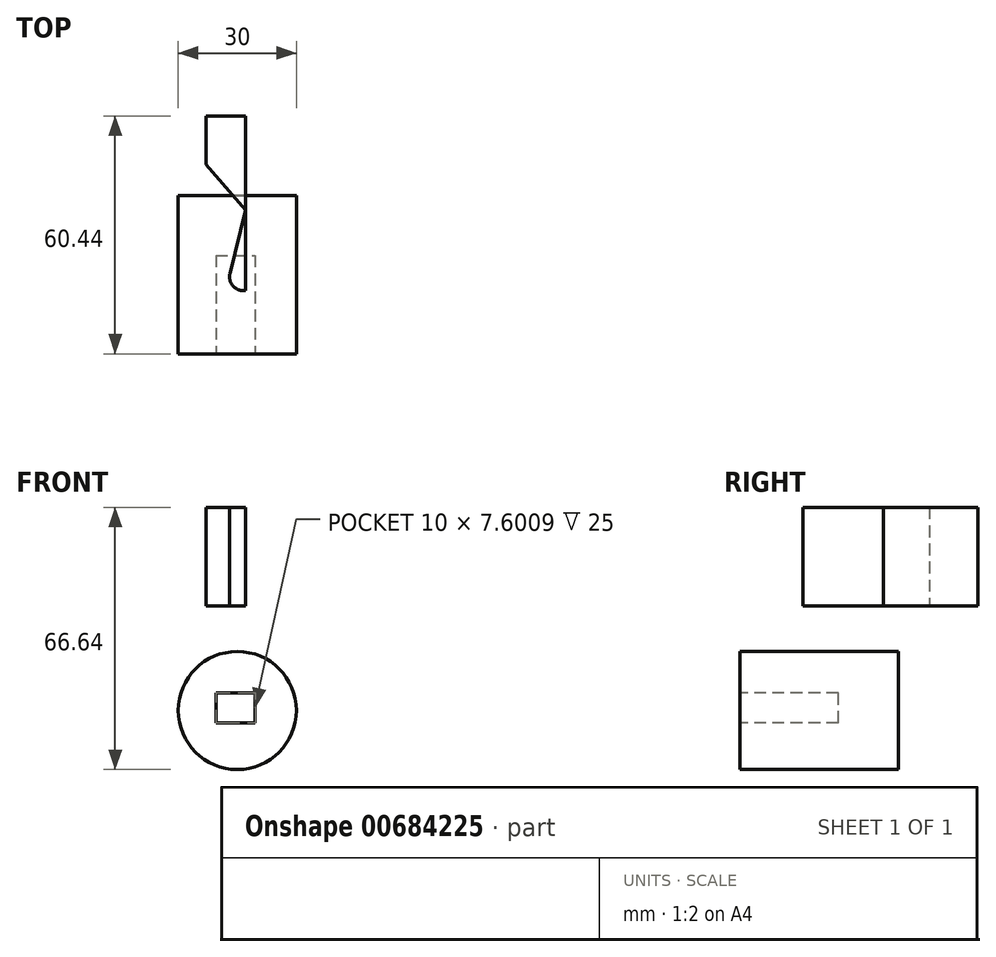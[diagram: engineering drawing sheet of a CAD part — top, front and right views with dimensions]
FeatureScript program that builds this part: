
annotation { "Feature Type Name" : "Feature", "Feature Type Description" : "" }
export const myFeature = defineFeature(function(context is Context, id is Id, definition is map)
    precondition{}
    {
        {
            var Q0;
            Q0=qCreatedBy(makeId("Top.planeOp"),FACE);
            var sketch = newSketch(context, id + "F0", { "sketchPlane" : qUnion([Q0])});
            skLineSegment(sketch, "E0.bottom", {"start": v(-77.17, 20.24) * mm, "end": v(-67.17, 20.24) * mm});
            skLineSegment(sketch, "E0.top", {"start": v(-77.17, -24.16) * mm, "end": v(-67.17, -24.16) * mm});
            skLineSegment(sketch, "E0.left", {"start": v(-77.17, 20.24) * mm, "end": v(-77.17, -24.16) * mm});
            skLineSegment(sketch, "E0.right", {"start": v(-67.17, 20.24) * mm, "end": v(-67.17, -24.16) * mm});
            skLineSegment(sketch, "E1", {"start": v(-77.17, 7.9) * mm, "end": v(-67.17, -3.72) * mm});
            skLineSegment(sketch, "E2", {"start": v(-67.17, -3.72) * mm, "end": v(-72.17, -24.16) * mm});
            skSolve(sketch);
        }
        {
            var Q0;
            {var subQ0=sQuery(id+"F0.wireOp",EDGE,"E0.bottom");Q0=makeQuery(id+"F0.imprint","IMPRINT",FACE,{"disambiguationData":[TD([[makeQuery(id+"F0.imprint","IMPRINT",EDGE,{"derivedFrom":subQ0}),-1.0]])]});}
            var Q1;
            {var subQ3=sQuery(id+"F0.wireOp",EDGE,"E2");Q1=makeQuery(id+"F0.imprint","IMPRINT",FACE,{"disambiguationData":[TD([[makeQuery(id+"F0.imprint","IMPRINT",EDGE,{"derivedFrom":subQ3}),1.0]])]});}
            extrude(context, id + "F1", {"entities" : qUnion([Q0, Q1]), "depth" : 25 * mm, "offsetDistance" : 25 * mm});
        }
        {
            var Q0;
            Q0=makeQuery(id+"F1.opExtrude","SWEPT_EDGE",EDGE,{"disambiguationData":[OSD([sQuery(id+"F0.wireOp",EDGE,"E0.top"),sQuery(id+"F0.wireOp",EDGE,"E2")])]});
            fillet(context, id + "F2", {"entities" : qUnion([Q0]), "radius" : 3.55 * mm, "tangentPropagation" : true, "allowEdgeOverflow" : false});
        }
        {
            var Q0;
            Q0=qCreatedBy(makeId("Front.planeOp"),FACE);
            var sketch = newSketch(context, id + "F3", { "sketchPlane" : qUnion([Q0])});
            skCircle(sketch, "E3", {"center": v(-69.23, -26.64) * mm, "radius": 15 * mm});
            skSolve(sketch);
        }
        {
            var Q0;
            Q0 = qSketchRegion(id + "F3", true);
            extrude(context, id + "F4", {"entities" : qUnion([Q0]), "depth" : 40.2 * mm, "offsetDistance" : 25 * mm});
        }
        {
            var Q0;
            Q0=makeQuery(id+"F4.opExtrude","CAP_FACE",FACE,{"disambiguationData":[OSD([sQuery(id+"F3.wireOp",EDGE,"E3")])],"isStart":false});
            var sketch = newSketch(context, id + "F5", { "sketchPlane" : qUnion([Q0])});
            skLineSegment(sketch, "E4.bottom", {"start": v(-74.65, -29.74) * mm, "end": v(-64.65, -29.74) * mm});
            skLineSegment(sketch, "E4.top", {"start": v(-74.65, -22.14) * mm, "end": v(-64.65, -22.14) * mm});
            skLineSegment(sketch, "E4.left", {"start": v(-74.65, -29.74) * mm, "end": v(-74.65, -22.14) * mm});
            skLineSegment(sketch, "E4.right", {"start": v(-64.65, -29.74) * mm, "end": v(-64.65, -22.14) * mm});
            skSolve(sketch);
        }
        {
            var Q0;
            Q0=makeQuery(id+"F5.imprint","IMPRINT",FACE,{"disambiguationData":[TD([[makeQuery(id+"F5.imprint","IMPRINT",EDGE,{"derivedFrom":sQuery(id+"F5.wireOp",EDGE,"E4.bottom")}),1.0]])]});
            extrude(context, id + "F6", {"entities" : qUnion([Q0]), "operationType" : NewBodyOperationType.REMOVE, "oppositeDirection" : true, "depth" : 25 * mm, "offsetDistance" : 25 * mm});
        }
    });
